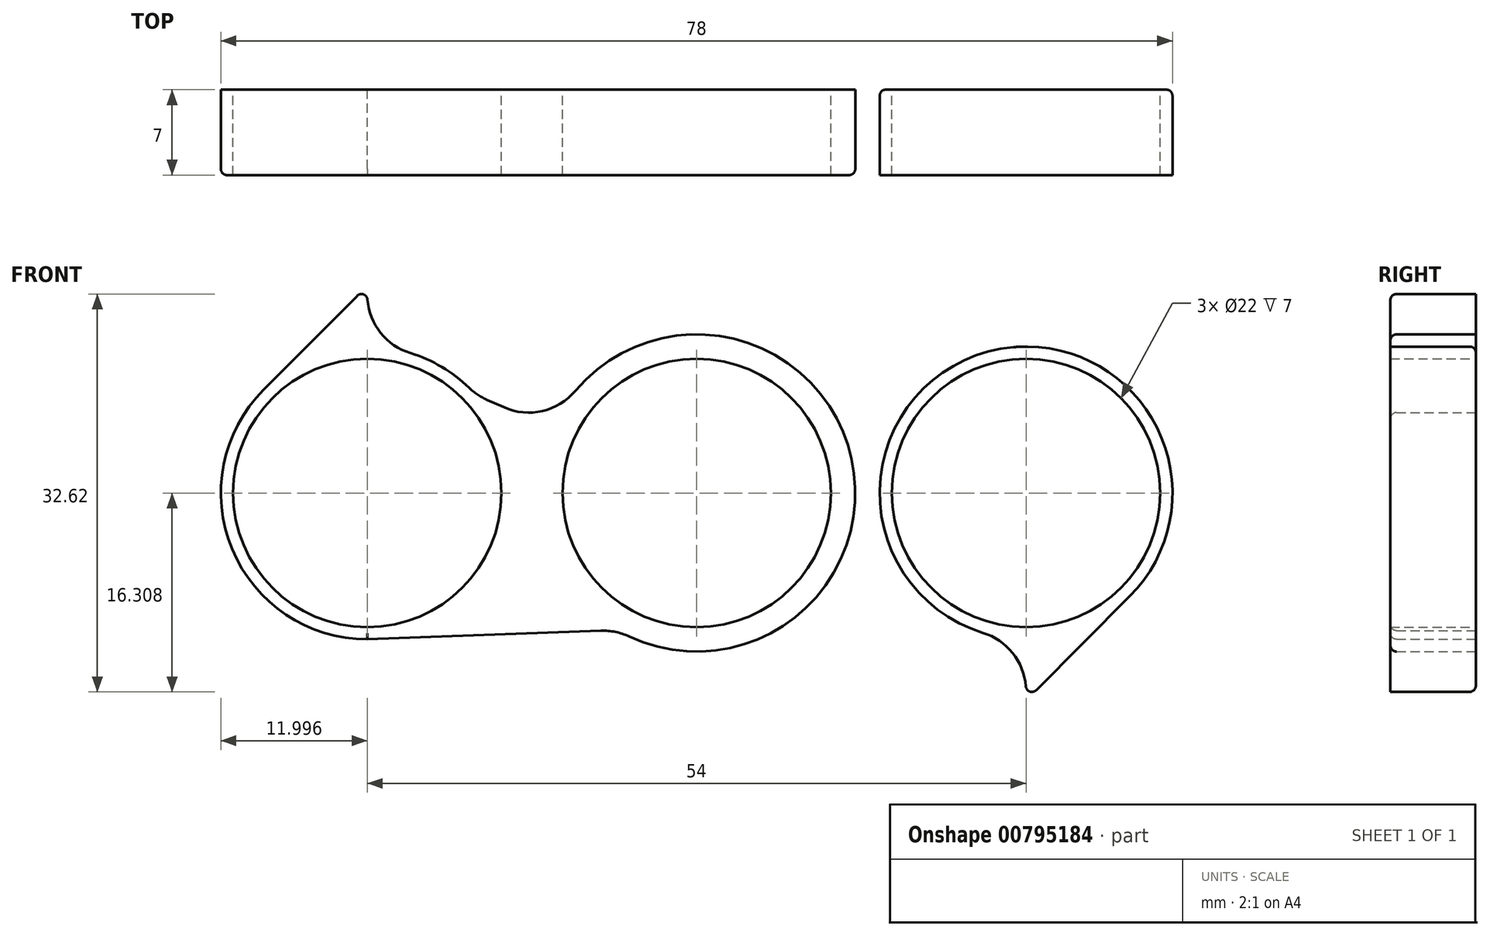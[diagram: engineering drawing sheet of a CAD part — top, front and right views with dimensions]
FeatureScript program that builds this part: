
annotation { "Feature Type Name" : "Feature", "Feature Type Description" : "" }
export const myFeature = defineFeature(function(context is Context, id is Id, definition is map)
    precondition{}
    {
        {
            var Q0;
            Q0=qCreatedBy(makeId("Front.planeOp"),FACE);
            var sketch = newSketch(context, id + "F0", { "sketchPlane" : qUnion([Q0])});
            skCircle(sketch, "E0", {"center": v(-97.65, 25.99) * mm, "radius": 11 * mm});
            skCircle(sketch, "E1", {"center": v(-124.65, 25.99) * mm, "radius": 11 * mm});
            skCircle(sketch, "E2", {"center": v(-70.65, 25.99) * mm, "radius": 11 * mm});
            skCircle(sketch, "E3.0", {"center": v(-124.65, 25.99) * mm, "radius": 12 * mm});
            skCircle(sketch, "E4.0", {"center": v(-70.65, 25.99) * mm, "radius": 12 * mm});
            skPoint(sketch, "E5", {"position": v(-124.65, 37.99) * mm});
            skPoint(sketch, "E6", {"position": v(-70.65, 13.99) * mm});
            skPoint(sketch, "E7", {"position": v(-107.7, 30.46) * mm});
            skPoint(sketch, "E8", {"position": v(-87.6, 21.52) * mm});
            skLineSegment(sketch, "E9", {"start": v(-121.68, 36.67) * mm, "end": v(-107.7, 30.46) * mm});
            skLineSegment(sketch, "E10", {"start": v(-73.62, 15.3) * mm, "end": v(-87.6, 21.52) * mm});
            skLineSegment(sketch, "E11", {"start": v(-70.65, 37.99) * mm, "end": v(-97.65, 36.99) * mm});
            skLineSegment(sketch, "E12", {"start": v(-124.65, 13.99) * mm, "end": v(-97.65, 14.99) * mm});
            skCircle(sketch, "E13.0", {"center": v(-97.65, 25.99) * mm, "radius": 13 * mm});
            skLineSegment(sketch, "E14", {"start": v(-124.65, 41.24) * mm, "end": v(-124.65, 42.99) * mm});
            skLineSegment(sketch, "E15", {"start": v(-70.65, 10.74) * mm, "end": v(-70.65, 8.99) * mm});
            skLineSegment(sketch, "E16", {"start": v(-124.65, 42.99) * mm, "end": v(-133.15, 34.46) * mm});
            skLineSegment(sketch, "E17", {"start": v(-70.65, 8.99) * mm, "end": v(-62.15, 17.52) * mm});
            skArc(sketch, "E18.filletArc", {"start": v(-70.65, 10.74) * mm, "mid": v(-71.46, 13.46) * mm, "end": v(-73.62, 15.3) * mm});
            skArc(sketch, "E19.filletArc", {"start": v(-124.65, 41.24) * mm, "mid": v(-123.85, 38.51) * mm, "end": v(-121.68, 36.67) * mm});
            skSolve(sketch);
        }
        {
            var Q0;
            {var subQ0=sQuery(id+"F0.wireOp",EDGE,"E9");var subQ9=sQuery(id+"F0.wireOp",EDGE,"E1");var subQ12=makeQuery(id+"F0.imprint","INTERSECT",VERTEX,{"disambiguationData":[OD(0.0)],"derivedFrom":[subQ9,subQ0]});Q0=makeQuery(id+"F0.imprint","IMPRINT",FACE,{"disambiguationData":[TD([[makeQuery(id+"F0.imprint","IMPRINT",EDGE,{"disambiguationData":[TD([[subQ12,-1.0]])],"derivedFrom":subQ9}),-1.0]])]});}
            var Q1;
            {var subQ0=sQuery(id+"F0.wireOp",EDGE,"E9");var subQ1=sQuery(id+"F0.wireOp",EDGE,"E3.0");var subQ2=makeQuery(id+"F0.imprint","INTERSECT",VERTEX,{"derivedFrom":[subQ1,subQ0]});Q1=makeQuery(id+"F0.imprint","IMPRINT",FACE,{"disambiguationData":[TD([[makeQuery(id+"F0.imprint","IMPRINT",EDGE,{"disambiguationData":[TD([[subQ2,1.0]])],"derivedFrom":subQ1}),-1.0]])]});}
            var Q2;
            {var subQ4=sQuery(id+"F0.wireOp",EDGE,"E14");Q2=makeQuery(id+"F0.imprint","IMPRINT",FACE,{"disambiguationData":[TD([[makeQuery(id+"F0.imprint","IMPRINT",EDGE,{"derivedFrom":subQ4}),1.0]])]});}
            var Q3;
            {var subQ0=sQuery(id+"F0.wireOp",EDGE,"E9");var subQ3=sQuery(id+"F0.wireOp",EDGE,"E1");var subQ7=makeQuery(id+"F0.imprint","INTERSECT",VERTEX,{"disambiguationData":[OD(0.0)],"derivedFrom":[subQ3,subQ0]});Q3=makeQuery(id+"F0.imprint","IMPRINT",FACE,{"disambiguationData":[TD([[makeQuery(id+"F0.imprint","IMPRINT",EDGE,{"disambiguationData":[TD([[subQ7,1.0]])],"derivedFrom":subQ3}),-1.0]])]});}
            var Q4;
            {var subQ0=sQuery(id+"F0.wireOp",EDGE,"E9");var subQ1=sQuery(id+"F0.wireOp",EDGE,"E0");var subQ2=makeQuery(id+"F0.imprint","INTERSECT",VERTEX,{"derivedFrom":[subQ1,subQ0]});Q4=makeQuery(id+"F0.imprint","IMPRINT",FACE,{"disambiguationData":[TD([[makeQuery(id+"F0.imprint","IMPRINT",EDGE,{"disambiguationData":[TD([[subQ2,1.0]])],"derivedFrom":subQ1}),-1.0]])]});}
            var Q5;
            {var subQ0=sQuery(id+"F0.wireOp",EDGE,"E9");var subQ1=sQuery(id+"F0.wireOp",EDGE,"E0");var subQ2=makeQuery(id+"F0.imprint","INTERSECT",VERTEX,{"derivedFrom":[subQ1,subQ0]});Q5=makeQuery(id+"F0.imprint","IMPRINT",FACE,{"disambiguationData":[TD([[makeQuery(id+"F0.imprint","IMPRINT",EDGE,{"disambiguationData":[TD([[subQ2,-1.0]])],"derivedFrom":subQ1}),-1.0]])]});}
            var Q6;
            {var subQ0=sQuery(id+"F0.wireOp",EDGE,"E10");var subQ1=sQuery(id+"F0.wireOp",EDGE,"E0");var subQ2=makeQuery(id+"F0.imprint","INTERSECT",VERTEX,{"derivedFrom":[subQ1,subQ0]});Q6=makeQuery(id+"F0.imprint","IMPRINT",FACE,{"disambiguationData":[TD([[makeQuery(id+"F0.imprint","IMPRINT",EDGE,{"disambiguationData":[TD([[subQ2,-1.0]])],"derivedFrom":subQ1}),-1.0]])]});}
            var Q7;
            {var subQ0=sQuery(id+"F0.wireOp",EDGE,"E10");var subQ1=sQuery(id+"F0.wireOp",EDGE,"E0");var subQ2=makeQuery(id+"F0.imprint","INTERSECT",VERTEX,{"derivedFrom":[subQ1,subQ0]});Q7=makeQuery(id+"F0.imprint","IMPRINT",FACE,{"disambiguationData":[TD([[makeQuery(id+"F0.imprint","IMPRINT",EDGE,{"disambiguationData":[TD([[subQ2,1.0]])],"derivedFrom":subQ1}),-1.0]])]});}
            var Q8;
            {var subQ0=sQuery(id+"F0.wireOp",EDGE,"E11");var subQ1=sQuery(id+"F0.wireOp",EDGE,"E4.0");var subQ2=makeQuery(id+"F0.imprint","INTERSECT",VERTEX,{"disambiguationData":[OD(1.0)],"derivedFrom":[subQ1,subQ0]});Q8=makeQuery(id+"F0.imprint","IMPRINT",FACE,{"disambiguationData":[TD([[makeQuery(id+"F0.imprint","IMPRINT",EDGE,{"disambiguationData":[TD([[subQ2,-1.0]])],"derivedFrom":subQ1}),-1.0]])]});}
            var Q9;
            {var subQ6=sQuery(id+"F0.wireOp",EDGE,"E10");var subQ8=sQuery(id+"F0.wireOp",EDGE,"E2");var subQ11=makeQuery(id+"F0.imprint","INTERSECT",VERTEX,{"disambiguationData":[OD(0.0)],"derivedFrom":[subQ8,subQ6]});Q9=makeQuery(id+"F0.imprint","IMPRINT",FACE,{"disambiguationData":[TD([[makeQuery(id+"F0.imprint","IMPRINT",EDGE,{"disambiguationData":[TD([[subQ11,-1.0]])],"derivedFrom":subQ8}),-1.0]])]});}
            var Q10;
            {var subQ1=sQuery(id+"F0.wireOp",EDGE,"E10");var subQ3=sQuery(id+"F0.wireOp",EDGE,"E2");var subQ4=makeQuery(id+"F0.imprint","INTERSECT",VERTEX,{"disambiguationData":[OD(0.0)],"derivedFrom":[subQ3,subQ1]});Q10=makeQuery(id+"F0.imprint","IMPRINT",FACE,{"disambiguationData":[TD([[makeQuery(id+"F0.imprint","IMPRINT",EDGE,{"disambiguationData":[TD([[subQ4,1.0]])],"derivedFrom":subQ3}),-1.0]])]});}
            var Q11;
            {var subQ4=sQuery(id+"F0.wireOp",EDGE,"E15");Q11=makeQuery(id+"F0.imprint","IMPRINT",FACE,{"disambiguationData":[TD([[makeQuery(id+"F0.imprint","IMPRINT",EDGE,{"derivedFrom":subQ4}),1.0]])]});}
            extrude(context, id + "F1", {"entities" : qUnion([Q0, Q1, Q2, Q3, Q4, Q5, Q6, Q7, Q8, Q9, Q10, Q11]), "depth" : 7 * mm, "offsetDistance" : 25 * mm});
        }
        {
            var Q0;
            Q0=makeQuery(id+"F1.opExtrude","SWEPT_EDGE",EDGE,{"disambiguationData":[OSD([sQuery(id+"F0.wireOp",EDGE,"E3.0"),sQuery(id+"F0.wireOp",EDGE,"E9")])]});
            var Q1;
            Q1=makeQuery(id+"F1.opExtrude","SWEPT_EDGE",EDGE,{"disambiguationData":[OSD([sQuery(id+"F0.wireOp",EDGE,"E9"),sQuery(id+"F0.wireOp",EDGE,"E13.0")])]});
            var Q2;
            Q2=makeQuery(id+"F1.opExtrude","SWEPT_EDGE",EDGE,{"disambiguationData":[OSD([sQuery(id+"F0.wireOp",EDGE,"E11"),sQuery(id+"F0.wireOp",EDGE,"E13.0")])]});
            var Q3;
            Q3=makeQuery(id+"F1.opExtrude","SWEPT_EDGE",EDGE,{"disambiguationData":[OSD([sQuery(id+"F0.wireOp",EDGE,"E12"),sQuery(id+"F0.wireOp",EDGE,"E13.0")])]});
            var Q4;
            Q4=makeQuery(id+"F1.opExtrude","SWEPT_EDGE",EDGE,{"disambiguationData":[OSD([sQuery(id+"F0.wireOp",EDGE,"E10"),sQuery(id+"F0.wireOp",EDGE,"E13.0")])]});
            var Q5;
            Q5=makeQuery(id+"F1.opExtrude","SWEPT_EDGE",EDGE,{"disambiguationData":[OSD([sQuery(id+"F0.wireOp",EDGE,"E4.0"),sQuery(id+"F0.wireOp",EDGE,"E10")])]});
            var Q6;
            Q6=makeQuery(id+"F1.opExtrude","SWEPT_EDGE",EDGE,{"disambiguationData":[OSD([sQuery(id+"F0.wireOp",EDGE,"E4.0"),sQuery(id+"F0.wireOp",EDGE,"E18.filletArc")])]});
            var Q7;
            Q7=makeQuery(id+"F1.opExtrude","SWEPT_EDGE",EDGE,{"disambiguationData":[OSD([sQuery(id+"F0.wireOp",EDGE,"E3.0"),sQuery(id+"F0.wireOp",EDGE,"E19.filletArc")])]});
            fillet(context, id + "F2", {"entities" : qUnion([Q0, Q1, Q2, Q3, Q4, Q5, Q6, Q7]), "radius" : 5 * mm, "tangentPropagation" : true, "allowEdgeOverflow" : false});
        }
        {
            var Q0;
            Q0=makeQuery(id+"F1.opExtrude","SWEPT_EDGE",EDGE,{"disambiguationData":[OSD([sQuery(id+"F0.wireOp",EDGE,"E14"),sQuery(id+"F0.wireOp",EDGE,"E16")])]});
            var Q1;
            Q1=makeQuery(id+"F1.opExtrude","SWEPT_EDGE",EDGE,{"disambiguationData":[OSD([sQuery(id+"F0.wireOp",EDGE,"E15"),sQuery(id+"F0.wireOp",EDGE,"E17")])]});
            fillet(context, id + "F3", {"entities" : qUnion([Q0, Q1]), "radius" : .5 * mm, "tangentPropagation" : true, "allowEdgeOverflow" : false});
        }
        {
            var Q0;
            Q0=makeQuery(id+"F1.opExtrude","CAP_EDGE",EDGE,{"disambiguationData":[OSD([sQuery(id+"F0.wireOp",EDGE,"E12")])],"isStart":false});
            var Q1;
            {var subQ0=sQuery(id+"F0.wireOp",EDGE,"E3.0");Q1=makeQuery(id+"F1.opExtrude","CAP_EDGE",EDGE,{"disambiguationData":[OSD([subQ0]),TDD([makeQuery(id+"F0.imprint","IMPRINT",EDGE,{"disambiguationData":[TD([[makeQuery(id+"F0.imprint","INTERSECT",VERTEX,{"disambiguationData":[OD(0.0)],"derivedFrom":[subQ0,sQuery(id+"F0.wireOp",EDGE,"E12")]}),1.0]])],"derivedFrom":subQ0})])],"isStart":false});}
            var Q2;
            Q2=makeQuery(id+"F1.opExtrude","CAP_EDGE",EDGE,{"disambiguationData":[OSD([sQuery(id+"F0.wireOp",EDGE,"E16")])],"isStart":false});
            var Q3;
            Q3=makeQuery(id+"F1.opExtrude","CAP_EDGE",EDGE,{"disambiguationData":[OSD([sQuery(id+"F0.wireOp",EDGE,"E11")])],"isStart":true});
            var Q4;
            {var subQ0=sQuery(id+"F0.wireOp",EDGE,"E4.0");Q4=makeQuery(id+"F1.opExtrude","CAP_EDGE",EDGE,{"disambiguationData":[OSD([subQ0]),TDD([makeQuery(id+"F0.imprint","IMPRINT",EDGE,{"disambiguationData":[TD([[makeQuery(id+"F0.imprint","INTERSECT",VERTEX,{"disambiguationData":[OD(0.0)],"derivedFrom":[subQ0,sQuery(id+"F0.wireOp",EDGE,"E11")]}),1.0]])],"derivedFrom":subQ0})])],"isStart":true});}
            var Q5;
            Q5=makeQuery(id+"F1.opExtrude","CAP_EDGE",EDGE,{"disambiguationData":[OSD([sQuery(id+"F0.wireOp",EDGE,"E17")])],"isStart":true});
            fillet(context, id + "F4", {"entities" : qUnion([Q0, Q1, Q2, Q3, Q4, Q5]), "radius" : .5 * mm, "tangentPropagation" : true, "allowEdgeOverflow" : false});
        }
    });
